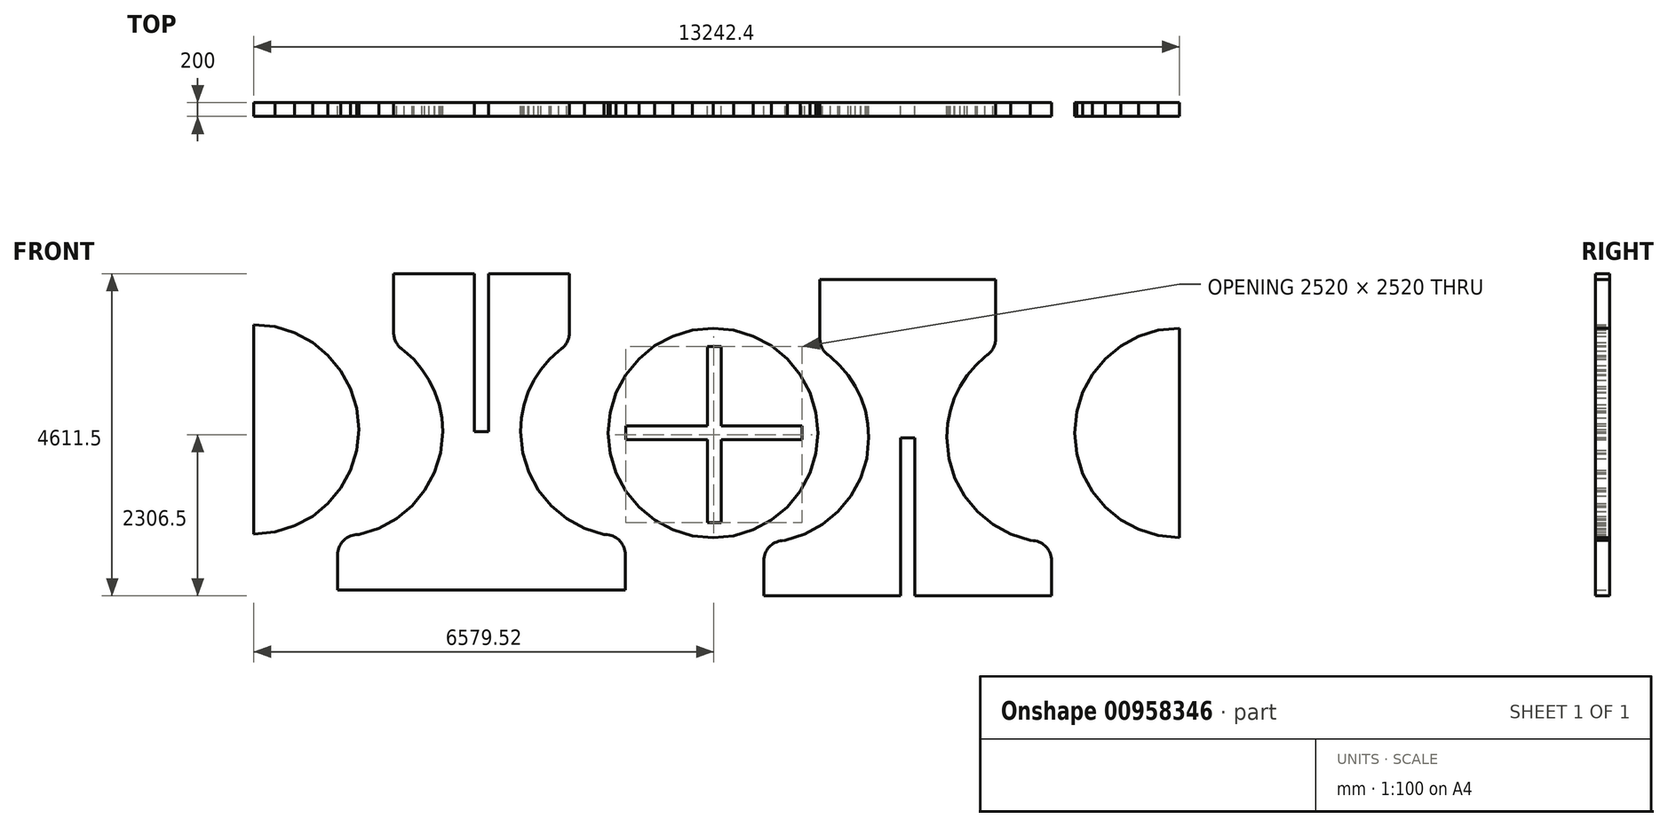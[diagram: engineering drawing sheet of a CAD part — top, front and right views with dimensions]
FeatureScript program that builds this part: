
annotation { "Feature Type Name" : "Feature", "Feature Type Description" : "" }
export const myFeature = defineFeature(function(context is Context, id is Id, definition is map)
    precondition{}
    {
        {
            var Q0;
            Q0=qCreatedBy(makeId("Front.planeOp"),FACE);
            var sketch = newSketch(context, id + "F0", { "sketchPlane" : qUnion([Q0])});
            skLineSegment(sketch, "E0", {"start": v(13749.06, 1599.41) * mm, "end": v(13456.43, 1570.6) * mm});
            skLineSegment(sketch, "E1", {"start": v(13456.43, 1570.6) * mm, "end": v(13175.04, 1485.23) * mm});
            skLineSegment(sketch, "E2", {"start": v(13175.04, 1485.23) * mm, "end": v(12915.7, 1346.62) * mm});
            skLineSegment(sketch, "E3", {"start": v(12915.7, 1346.62) * mm, "end": v(12688.4, 1160.07) * mm});
            skLineSegment(sketch, "E4", {"start": v(12688.4, 1160.07) * mm, "end": v(12501.86, 932.77) * mm});
            skLineSegment(sketch, "E5", {"start": v(12501.86, 932.77) * mm, "end": v(12363.24, 673.44) * mm});
            skLineSegment(sketch, "E6", {"start": v(12363.24, 673.44) * mm, "end": v(12277.89, 392.05) * mm});
            skLineSegment(sketch, "E7", {"start": v(12277.89, 392.05) * mm, "end": v(12249.06, 99.41) * mm});
            skLineSegment(sketch, "E8", {"start": v(12249.06, 99.41) * mm, "end": v(12277.89, -193.22) * mm});
            skLineSegment(sketch, "E9", {"start": v(12277.89, -193.22) * mm, "end": v(12363.24, -474.61) * mm});
            skLineSegment(sketch, "E10", {"start": v(12363.24, -474.61) * mm, "end": v(12501.86, -733.94) * mm});
            skLineSegment(sketch, "E11", {"start": v(12501.86, -733.94) * mm, "end": v(12688.4, -961.25) * mm});
            skLineSegment(sketch, "E12", {"start": v(12688.4, -961.25) * mm, "end": v(12915.7, -1147.8) * mm});
            skLineSegment(sketch, "E13", {"start": v(12915.7, -1147.8) * mm, "end": v(13175.04, -1286.4) * mm});
            skLineSegment(sketch, "E14", {"start": v(13175.04, -1286.4) * mm, "end": v(13456.43, -1371.76) * mm});
            skLineSegment(sketch, "E15", {"start": v(13456.43, -1371.76) * mm, "end": v(13749.06, -1400.59) * mm});
            skLineSegment(sketch, "E16", {"start": v(13749.06, -1400.59) * mm, "end": v(14041.7, -1371.76) * mm});
            skLineSegment(sketch, "E17", {"start": v(14041.7, -1371.76) * mm, "end": v(14323.09, -1286.4) * mm});
            skLineSegment(sketch, "E18", {"start": v(14323.09, -1286.4) * mm, "end": v(14582.42, -1147.8) * mm});
            skLineSegment(sketch, "E19", {"start": v(14582.42, -1147.8) * mm, "end": v(14809.72, -961.25) * mm});
            skLineSegment(sketch, "E20", {"start": v(14809.72, -961.25) * mm, "end": v(14996.27, -733.94) * mm});
            skLineSegment(sketch, "E21", {"start": v(14996.27, -733.94) * mm, "end": v(15134.88, -474.61) * mm});
            skLineSegment(sketch, "E22", {"start": v(15134.88, -474.61) * mm, "end": v(15220.24, -193.22) * mm});
            skLineSegment(sketch, "E23", {"start": v(15220.24, -193.22) * mm, "end": v(15249.06, 99.41) * mm});
            skLineSegment(sketch, "E24", {"start": v(15249.06, 99.41) * mm, "end": v(15220.24, 392.05) * mm});
            skLineSegment(sketch, "E25", {"start": v(15220.24, 392.05) * mm, "end": v(15134.88, 673.44) * mm});
            skLineSegment(sketch, "E26", {"start": v(15134.88, 673.44) * mm, "end": v(14996.27, 932.77) * mm});
            skLineSegment(sketch, "E27", {"start": v(14996.27, 932.77) * mm, "end": v(14809.72, 1160.07) * mm});
            skLineSegment(sketch, "E28", {"start": v(14809.72, 1160.07) * mm, "end": v(14582.42, 1346.62) * mm});
            skLineSegment(sketch, "E29", {"start": v(14582.42, 1346.62) * mm, "end": v(14323.09, 1485.23) * mm});
            skLineSegment(sketch, "E30", {"start": v(14323.09, 1485.23) * mm, "end": v(14041.7, 1570.6) * mm});
            skLineSegment(sketch, "E31", {"start": v(14041.7, 1570.6) * mm, "end": v(13749.06, 1599.41) * mm});
            skLineSegment(sketch, "E32", {"start": v(8382, -1384) * mm, "end": v(8382, -2147.09) * mm});
            skLineSegment(sketch, "E33", {"start": v(8382, -2147.09) * mm, "end": v(12496, -2147.09) * mm});
            skLineSegment(sketch, "E34", {"start": v(12496, -2147.09) * mm, "end": v(12496, -1384) * mm});
            skLineSegment(sketch, "E35", {"start": v(12496, -1384) * mm, "end": v(12493.23, -1383.62) * mm});
            skLineSegment(sketch, "E36", {"start": v(12493.23, -1383.62) * mm, "end": v(12191.41, -1352.68) * mm});
            skLineSegment(sketch, "E37", {"start": v(12191.41, -1352.68) * mm, "end": v(11910.33, -1264.99) * mm});
            skLineSegment(sketch, "E38", {"start": v(11910.33, -1264.99) * mm, "end": v(11656, -1126.55) * mm});
            skLineSegment(sketch, "E39", {"start": v(11656, -1126.55) * mm, "end": v(11434.43, -943.39) * mm});
            skLineSegment(sketch, "E40", {"start": v(11434.43, -943.39) * mm, "end": v(11251.63, -721.5) * mm});
            skLineSegment(sketch, "E41", {"start": v(11251.63, -721.5) * mm, "end": v(11113.62, -466.91) * mm});
            skLineSegment(sketch, "E42", {"start": v(11113.62, -466.91) * mm, "end": v(11026.4, -185.63) * mm});
            skLineSegment(sketch, "E43", {"start": v(11026.4, -185.63) * mm, "end": v(10996, 116.35) * mm});
            skLineSegment(sketch, "E44", {"start": v(10996, 116.35) * mm, "end": v(11008.82, 313.32) * mm});
            skLineSegment(sketch, "E45", {"start": v(11008.82, 313.32) * mm, "end": v(11046.2, 502.57) * mm});
            skLineSegment(sketch, "E46", {"start": v(11046.2, 502.57) * mm, "end": v(11106.52, 682.46) * mm});
            skLineSegment(sketch, "E47", {"start": v(11106.52, 682.46) * mm, "end": v(11188.17, 851.39) * mm});
            skLineSegment(sketch, "E48", {"start": v(11188.17, 851.39) * mm, "end": v(11289.53, 1007.73) * mm});
            skLineSegment(sketch, "E49", {"start": v(11289.53, 1007.73) * mm, "end": v(11408.98, 1149.88) * mm});
            skLineSegment(sketch, "E50", {"start": v(11408.98, 1149.88) * mm, "end": v(11544.9, 1276.22) * mm});
            skLineSegment(sketch, "E51", {"start": v(11544.9, 1276.22) * mm, "end": v(11695.67, 1385.13) * mm});
            skLineSegment(sketch, "E52", {"start": v(11695.67, 1385.13) * mm, "end": v(11695.67, 2379.75) * mm});
            skLineSegment(sketch, "E53", {"start": v(11695.67, 2379.75) * mm, "end": v(10538.87, 2379.75) * mm});
            skLineSegment(sketch, "E54", {"start": v(10538.87, 2379.75) * mm, "end": v(10538.87, 116.33) * mm});
            skLineSegment(sketch, "E55", {"start": v(10538.87, 116.33) * mm, "end": v(10338.87, 116.33) * mm});
            skLineSegment(sketch, "E56", {"start": v(10338.87, 116.33) * mm, "end": v(10338.87, 2379.75) * mm});
            skLineSegment(sketch, "E57", {"start": v(10338.87, 2379.75) * mm, "end": v(9182.34, 2379.75) * mm});
            skLineSegment(sketch, "E58", {"start": v(9182.34, 2379.75) * mm, "end": v(9182.34, 1385.13) * mm});
            skLineSegment(sketch, "E59", {"start": v(9182.34, 1385.13) * mm, "end": v(9333.11, 1276.22) * mm});
            skLineSegment(sketch, "E60", {"start": v(9333.11, 1276.22) * mm, "end": v(9469.03, 1149.88) * mm});
            skLineSegment(sketch, "E61", {"start": v(9469.03, 1149.88) * mm, "end": v(9588.48, 1007.73) * mm});
            skLineSegment(sketch, "E62", {"start": v(9588.48, 1007.73) * mm, "end": v(9689.84, 851.39) * mm});
            skLineSegment(sketch, "E63", {"start": v(9689.84, 851.39) * mm, "end": v(9771.49, 682.46) * mm});
            skLineSegment(sketch, "E64", {"start": v(9771.49, 682.46) * mm, "end": v(9831.81, 502.57) * mm});
            skLineSegment(sketch, "E65", {"start": v(9831.81, 502.57) * mm, "end": v(9869.2, 313.32) * mm});
            skLineSegment(sketch, "E66", {"start": v(9869.2, 313.32) * mm, "end": v(9882.01, 116.35) * mm});
            skLineSegment(sketch, "E67", {"start": v(9882.01, 116.35) * mm, "end": v(9851.6, -185.63) * mm});
            skLineSegment(sketch, "E68", {"start": v(9851.6, -185.63) * mm, "end": v(9764.4, -466.91) * mm});
            skLineSegment(sketch, "E69", {"start": v(9764.4, -466.91) * mm, "end": v(9626.38, -721.5) * mm});
            skLineSegment(sketch, "E70", {"start": v(9626.38, -721.5) * mm, "end": v(9443.58, -943.39) * mm});
            skLineSegment(sketch, "E71", {"start": v(9443.58, -943.39) * mm, "end": v(9222.01, -1126.55) * mm});
            skLineSegment(sketch, "E72", {"start": v(9222.01, -1126.55) * mm, "end": v(8967.68, -1264.99) * mm});
            skLineSegment(sketch, "E73", {"start": v(8967.68, -1264.99) * mm, "end": v(8686.6, -1352.68) * mm});
            skLineSegment(sketch, "E74", {"start": v(8686.6, -1352.68) * mm, "end": v(8384.78, -1383.62) * mm});
            skLineSegment(sketch, "E75", {"start": v(8384.78, -1383.62) * mm, "end": v(8382, -1384) * mm});
            skLineSegment(sketch, "E76", {"start": v(18591.2, -1468.68) * mm, "end": v(18591.2, -2231.75) * mm});
            skLineSegment(sketch, "E77", {"start": v(18591.2, -2231.75) * mm, "end": v(16634.05, -2231.75) * mm});
            skLineSegment(sketch, "E78", {"start": v(16634.05, -2231.75) * mm, "end": v(16634.05, 31.66) * mm});
            skLineSegment(sketch, "E79", {"start": v(16634.05, 31.66) * mm, "end": v(16434.05, 31.66) * mm});
            skLineSegment(sketch, "E80", {"start": v(16434.05, 31.66) * mm, "end": v(16434.05, -2231.75) * mm});
            skLineSegment(sketch, "E81", {"start": v(16434.05, -2231.75) * mm, "end": v(14477.2, -2231.75) * mm});
            skLineSegment(sketch, "E82", {"start": v(14477.2, -2231.75) * mm, "end": v(14477.2, -1468.68) * mm});
            skLineSegment(sketch, "E83", {"start": v(14477.2, -1468.68) * mm, "end": v(14479.98, -1468.29) * mm});
            skLineSegment(sketch, "E84", {"start": v(14479.98, -1468.29) * mm, "end": v(14781.8, -1437.34) * mm});
            skLineSegment(sketch, "E85", {"start": v(14781.8, -1437.34) * mm, "end": v(15062.87, -1349.65) * mm});
            skLineSegment(sketch, "E86", {"start": v(15062.87, -1349.65) * mm, "end": v(15317.2, -1211.21) * mm});
            skLineSegment(sketch, "E87", {"start": v(15317.2, -1211.21) * mm, "end": v(15538.77, -1028.05) * mm});
            skLineSegment(sketch, "E88", {"start": v(15538.77, -1028.05) * mm, "end": v(15721.56, -806.17) * mm});
            skLineSegment(sketch, "E89", {"start": v(15721.56, -806.17) * mm, "end": v(15859.57, -551.58) * mm});
            skLineSegment(sketch, "E90", {"start": v(15859.57, -551.58) * mm, "end": v(15946.79, -270.3) * mm});
            skLineSegment(sketch, "E91", {"start": v(15946.79, -270.3) * mm, "end": v(15977.2, 31.68) * mm});
            skLineSegment(sketch, "E92", {"start": v(15977.2, 31.68) * mm, "end": v(15964.38, 228.66) * mm});
            skLineSegment(sketch, "E93", {"start": v(15964.38, 228.66) * mm, "end": v(15927, 417.9) * mm});
            skLineSegment(sketch, "E94", {"start": v(15927, 417.9) * mm, "end": v(15866.67, 597.79) * mm});
            skLineSegment(sketch, "E95", {"start": v(15866.67, 597.79) * mm, "end": v(15785.02, 766.71) * mm});
            skLineSegment(sketch, "E96", {"start": v(15785.02, 766.71) * mm, "end": v(15683.67, 923.06) * mm});
            skLineSegment(sketch, "E97", {"start": v(15683.67, 923.06) * mm, "end": v(15564.22, 1065.2) * mm});
            skLineSegment(sketch, "E98", {"start": v(15564.22, 1065.2) * mm, "end": v(15428.3, 1191.54) * mm});
            skLineSegment(sketch, "E99", {"start": v(15428.3, 1191.54) * mm, "end": v(15277.53, 1300.46) * mm});
            skLineSegment(sketch, "E100", {"start": v(15277.53, 1300.46) * mm, "end": v(15277.53, 2295.08) * mm});
            skLineSegment(sketch, "E101", {"start": v(15277.53, 2295.08) * mm, "end": v(17790.86, 2295.08) * mm});
            skLineSegment(sketch, "E102", {"start": v(17790.86, 2295.08) * mm, "end": v(17790.86, 1300.46) * mm});
            skLineSegment(sketch, "E103", {"start": v(17790.86, 1300.46) * mm, "end": v(17640.1, 1191.54) * mm});
            skLineSegment(sketch, "E104", {"start": v(17640.1, 1191.54) * mm, "end": v(17504.17, 1065.2) * mm});
            skLineSegment(sketch, "E105", {"start": v(17504.17, 1065.2) * mm, "end": v(17384.73, 923.06) * mm});
            skLineSegment(sketch, "E106", {"start": v(17384.73, 923.06) * mm, "end": v(17283.37, 766.71) * mm});
            skLineSegment(sketch, "E107", {"start": v(17283.37, 766.71) * mm, "end": v(17201.72, 597.79) * mm});
            skLineSegment(sketch, "E108", {"start": v(17201.72, 597.79) * mm, "end": v(17141.4, 417.9) * mm});
            skLineSegment(sketch, "E109", {"start": v(17141.4, 417.9) * mm, "end": v(17104.02, 228.66) * mm});
            skLineSegment(sketch, "E110", {"start": v(17104.02, 228.66) * mm, "end": v(17091.2, 31.68) * mm});
            skLineSegment(sketch, "E111", {"start": v(17091.2, 31.68) * mm, "end": v(17121.6, -270.3) * mm});
            skLineSegment(sketch, "E112", {"start": v(17121.6, -270.3) * mm, "end": v(17208.82, -551.58) * mm});
            skLineSegment(sketch, "E113", {"start": v(17208.82, -551.58) * mm, "end": v(17346.83, -806.17) * mm});
            skLineSegment(sketch, "E114", {"start": v(17346.83, -806.17) * mm, "end": v(17529.63, -1028.05) * mm});
            skLineSegment(sketch, "E115", {"start": v(17529.63, -1028.05) * mm, "end": v(17751.2, -1211.21) * mm});
            skLineSegment(sketch, "E116", {"start": v(17751.2, -1211.21) * mm, "end": v(18005.53, -1349.65) * mm});
            skLineSegment(sketch, "E117", {"start": v(18005.53, -1349.65) * mm, "end": v(18286.6, -1437.34) * mm});
            skLineSegment(sketch, "E118", {"start": v(18286.6, -1437.34) * mm, "end": v(18588.42, -1468.29) * mm});
            skLineSegment(sketch, "E119", {"start": v(18588.42, -1468.29) * mm, "end": v(18591.2, -1468.68) * mm});
            skLineSegment(sketch, "E120", {"start": v(7182.52, 150.21) * mm, "end": v(7180.08, 1650.2) * mm});
            skLineSegment(sketch, "E121", {"start": v(7180.08, 1650.2) * mm, "end": v(7182.52, 1650.21) * mm});
            skLineSegment(sketch, "E122", {"start": v(7182.52, 1650.21) * mm, "end": v(7484.82, 1619.74) * mm});
            skLineSegment(sketch, "E123", {"start": v(7484.82, 1619.74) * mm, "end": v(7766.38, 1532.34) * mm});
            skLineSegment(sketch, "E124", {"start": v(7766.38, 1532.34) * mm, "end": v(8021.18, 1394.04) * mm});
            skLineSegment(sketch, "E125", {"start": v(8021.18, 1394.04) * mm, "end": v(8243.18, 1210.87) * mm});
            skLineSegment(sketch, "E126", {"start": v(8243.18, 1210.87) * mm, "end": v(8426.34, 988.88) * mm});
            skLineSegment(sketch, "E127", {"start": v(8426.34, 988.88) * mm, "end": v(8564.64, 734.08) * mm});
            skLineSegment(sketch, "E128", {"start": v(8564.64, 734.08) * mm, "end": v(8652.04, 452.51) * mm});
            skLineSegment(sketch, "E129", {"start": v(8652.04, 452.51) * mm, "end": v(8682.52, 150.21) * mm});
            skLineSegment(sketch, "E130", {"start": v(8682.52, 150.21) * mm, "end": v(8652.04, -152.09) * mm});
            skLineSegment(sketch, "E131", {"start": v(8652.04, -152.09) * mm, "end": v(8564.64, -433.66) * mm});
            skLineSegment(sketch, "E132", {"start": v(8564.64, -433.65) * mm, "end": v(8426.34, -688.45) * mm});
            skLineSegment(sketch, "E133", {"start": v(8426.34, -688.45) * mm, "end": v(8243.18, -910.45) * mm});
            skLineSegment(sketch, "E134", {"start": v(8243.18, -910.45) * mm, "end": v(8021.18, -1093.61) * mm});
            skLineSegment(sketch, "E135", {"start": v(8021.18, -1093.61) * mm, "end": v(7766.38, -1231.9) * mm});
            skLineSegment(sketch, "E136", {"start": v(7766.38, -1231.9) * mm, "end": v(7484.82, -1319.31) * mm});
            skLineSegment(sketch, "E137", {"start": v(7484.82, -1319.31) * mm, "end": v(7182.52, -1349.79) * mm});
            skLineSegment(sketch, "E138", {"start": v(7182.52, -1349.79) * mm, "end": v(7182.52, 150.21) * mm});
            skLineSegment(sketch, "E139", {"start": v(20420, 99.41) * mm, "end": v(20422.43, 1599.4) * mm});
            skLineSegment(sketch, "E140", {"start": v(20422.43, 1599.4) * mm, "end": v(20420, 1599.41) * mm});
            skLineSegment(sketch, "E141", {"start": v(20420, 1599.41) * mm, "end": v(20117.7, 1568.94) * mm});
            skLineSegment(sketch, "E142", {"start": v(20117.7, 1568.94) * mm, "end": v(19836.13, 1481.54) * mm});
            skLineSegment(sketch, "E143", {"start": v(19836.13, 1481.54) * mm, "end": v(19581.33, 1343.24) * mm});
            skLineSegment(sketch, "E144", {"start": v(19581.33, 1343.24) * mm, "end": v(19359.34, 1160.07) * mm});
            skLineSegment(sketch, "E145", {"start": v(19359.34, 1160.07) * mm, "end": v(19176.17, 938.08) * mm});
            skLineSegment(sketch, "E146", {"start": v(19176.17, 938.08) * mm, "end": v(19037.88, 683.28) * mm});
            skLineSegment(sketch, "E147", {"start": v(19037.88, 683.28) * mm, "end": v(18950.47, 401.71) * mm});
            skLineSegment(sketch, "E148", {"start": v(18950.47, 401.72) * mm, "end": v(18920, 99.41) * mm});
            skLineSegment(sketch, "E149", {"start": v(18920, 99.41) * mm, "end": v(18950.47, -202.89) * mm});
            skLineSegment(sketch, "E150", {"start": v(18950.47, -202.89) * mm, "end": v(19037.88, -484.46) * mm});
            skLineSegment(sketch, "E151", {"start": v(19037.88, -484.46) * mm, "end": v(19176.17, -739.25) * mm});
            skLineSegment(sketch, "E152", {"start": v(19176.17, -739.25) * mm, "end": v(19359.34, -961.25) * mm});
            skLineSegment(sketch, "E153", {"start": v(19359.34, -961.25) * mm, "end": v(19581.33, -1144.41) * mm});
            skLineSegment(sketch, "E154", {"start": v(19581.33, -1144.41) * mm, "end": v(19836.13, -1282.7) * mm});
            skLineSegment(sketch, "E155", {"start": v(19836.13, -1282.7) * mm, "end": v(20117.7, -1370.11) * mm});
            skLineSegment(sketch, "E156", {"start": v(20117.7, -1370.11) * mm, "end": v(20420, -1400.59) * mm});
            skLineSegment(sketch, "E157", {"start": v(20420, -1400.59) * mm, "end": v(20420, 99.41) * mm});
            skSolve(sketch);
        }
        {
            var Q0;
            Q0 = qSketchRegion(id + "F0", true);
            extrude(context, id + "F1", {"entities" : qUnion([Q0]), "depth" : 200 * mm, "offsetDistance" : 25 * mm});
        }
        {
            var Q0;
            Q0=makeQuery(id+"F1.opExtrude","SWEPT_EDGE",EDGE,{"disambiguationData":[OSD([sQuery(id+"F0.wireOp",EDGE,"E82"),sQuery(id+"F0.wireOp",EDGE,"E83")])]});
            var Q1;
            Q1=makeQuery(id+"F1.opExtrude","SWEPT_EDGE",EDGE,{"disambiguationData":[OSD([sQuery(id+"F0.wireOp",EDGE,"E76"),sQuery(id+"F0.wireOp",EDGE,"E119")])]});
            var Q2;
            Q2=makeQuery(id+"F1.opExtrude","SWEPT_EDGE",EDGE,{"disambiguationData":[OSD([sQuery(id+"F0.wireOp",EDGE,"E34"),sQuery(id+"F0.wireOp",EDGE,"E35")])]});
            var Q3;
            Q3=makeQuery(id+"F1.opExtrude","SWEPT_EDGE",EDGE,{"disambiguationData":[OSD([sQuery(id+"F0.wireOp",EDGE,"E32"),sQuery(id+"F0.wireOp",EDGE,"E75")])]});
            var Q4;
            Q4=makeQuery(id+"F1.opExtrude","SWEPT_EDGE",EDGE,{"disambiguationData":[OSD([sQuery(id+"F0.wireOp",EDGE,"E58"),sQuery(id+"F0.wireOp",EDGE,"E59")])]});
            var Q5;
            Q5=makeQuery(id+"F1.opExtrude","SWEPT_EDGE",EDGE,{"disambiguationData":[OSD([sQuery(id+"F0.wireOp",EDGE,"E51"),sQuery(id+"F0.wireOp",EDGE,"E52")])]});
            var Q6;
            Q6=makeQuery(id+"F1.opExtrude","SWEPT_EDGE",EDGE,{"disambiguationData":[OSD([sQuery(id+"F0.wireOp",EDGE,"E99"),sQuery(id+"F0.wireOp",EDGE,"E100")])]});
            var Q7;
            Q7=makeQuery(id+"F1.opExtrude","SWEPT_EDGE",EDGE,{"disambiguationData":[OSD([sQuery(id+"F0.wireOp",EDGE,"E102"),sQuery(id+"F0.wireOp",EDGE,"E103")])]});
            fillet(context, id + "F2", {"entities" : qUnion([Q0, Q1, Q2, Q3, Q4, Q5, Q6, Q7]), "radius" : 289.04 * mm, "tangentPropagation" : true, "allowEdgeOverflow" : false});
        }
        {
            var Q0;
            Q0=qCreatedBy(makeId("Front.planeOp"),FACE);
            var sketch = newSketch(context, id + "F3", { "sketchPlane" : qUnion([Q0])});
            skLineSegment(sketch, "E158.bottom", {"start": v(12499.6, 200) * mm, "end": v(15019.6, 200) * mm});
            skLineSegment(sketch, "E158.top", {"start": v(12499.6, 0) * mm, "end": v(15019.6, 0) * mm});
            skLineSegment(sketch, "E158.left", {"start": v(12499.6, 200) * mm, "end": v(12499.6, 0) * mm});
            skLineSegment(sketch, "E158.right", {"start": v(15019.6, 200) * mm, "end": v(15019.6, 0) * mm});
            skLineSegment(sketch, "E159.bottom", {"start": v(13669.43, -1185.25) * mm, "end": v(13669.43, 1334.75) * mm});
            skLineSegment(sketch, "E159.top", {"start": v(13869.43, -1185.25) * mm, "end": v(13869.43, 1334.75) * mm});
            skLineSegment(sketch, "E159.left", {"start": v(13669.43, -1185.25) * mm, "end": v(13869.43, -1185.25) * mm});
            skLineSegment(sketch, "E159.right", {"start": v(13669.43, 1334.75) * mm, "end": v(13869.43, 1334.75) * mm});
            skSolve(sketch);
        }
        {
            var Q0;
            Q0 = qSketchRegion(id + "F3", true);
            extrude(context, id + "F4", {"entities" : qUnion([Q0]), "operationType" : NewBodyOperationType.REMOVE, "depth" : 810 * mm, "offsetDistance" : 25 * mm});
        }
    });
